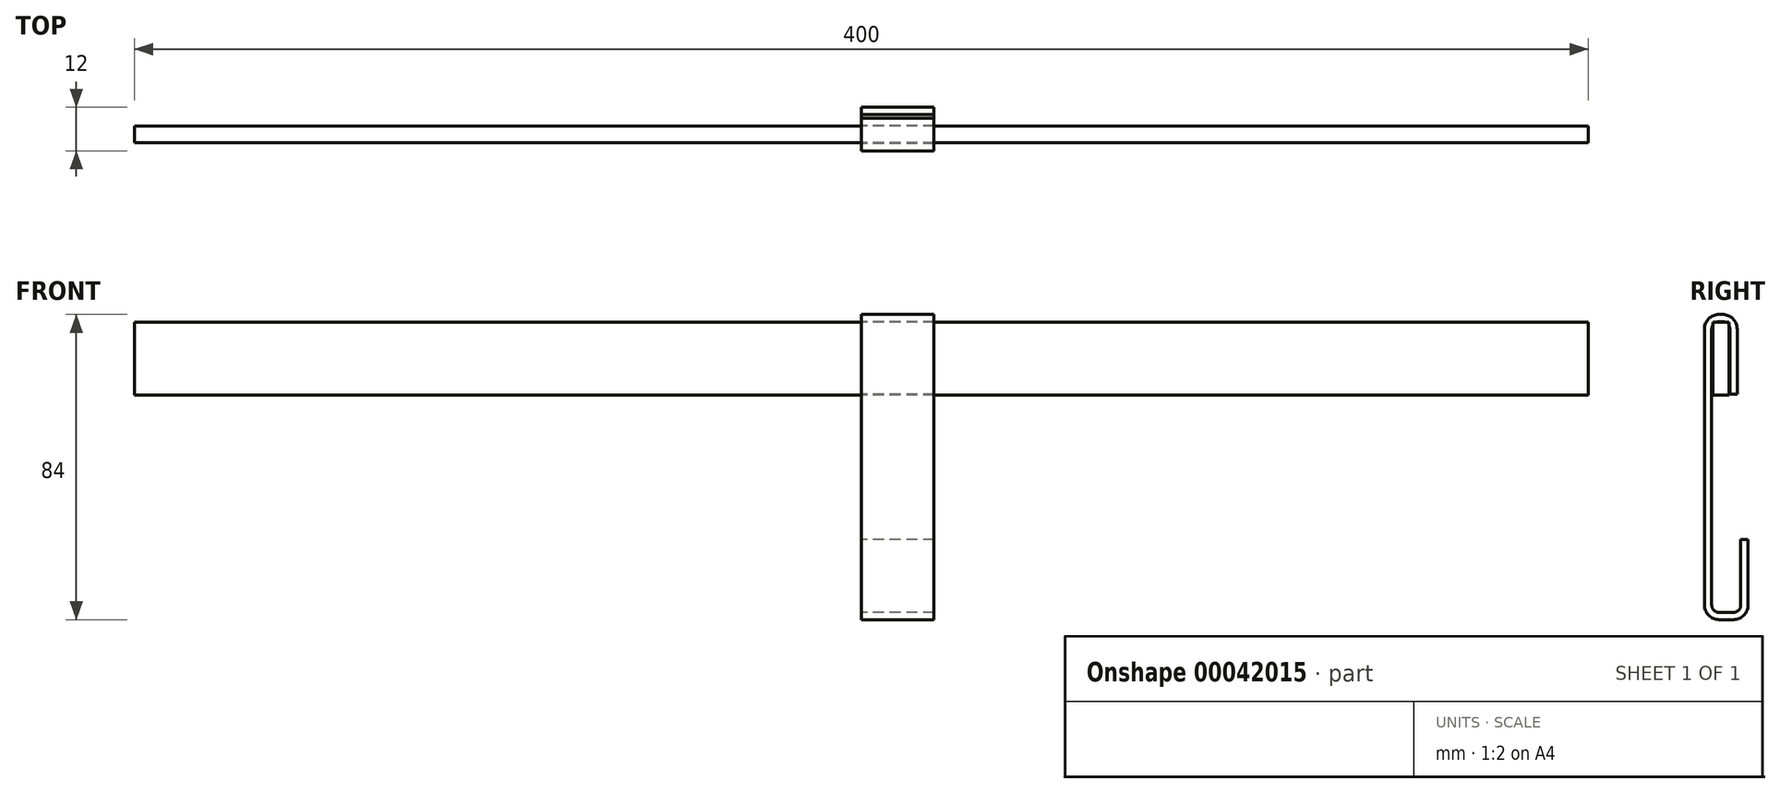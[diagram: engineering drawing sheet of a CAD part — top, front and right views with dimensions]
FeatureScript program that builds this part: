
annotation { "Feature Type Name" : "Feature", "Feature Type Description" : "" }
export const myFeature = defineFeature(function(context is Context, id is Id, definition is map)
    precondition{}
    {
        {
            var Q0;
            Q0=qCreatedBy(makeId("Right.planeOp"),FACE);
            var sketch = newSketch(context, id + "F0", { "sketchPlane" : qUnion([Q0])});
            skLineSegment(sketch, "E0", {"start": v(0, 0) * mm, "end": v(0, -80) * mm});
            skLineSegment(sketch, "E1", {"start": v(8, -80) * mm, "end": v(8, -60) * mm});
            skLineSegment(sketch, "E2", {"start": v(0, 0) * mm, "end": v(5, 0) * mm});
            skLineSegment(sketch, "E3", {"start": v(5, 0) * mm, "end": v(5, -20) * mm});
            skLineSegment(sketch, "E4", {"start": v(0, -80) * mm, "end": v(8, -80) * mm});
            skLineSegment(sketch, "E5.0", {"start": v(7, 2) * mm, "end": v(7, -20) * mm});
            skLineSegment(sketch, "E5.1", {"start": v(10, -82) * mm, "end": v(10, -60) * mm});
            skLineSegment(sketch, "E5.2", {"start": v(-2, -82) * mm, "end": v(10, -82) * mm});
            skLineSegment(sketch, "E5.3", {"start": v(-2, 2) * mm, "end": v(-2, -82) * mm});
            skLineSegment(sketch, "E5.4", {"start": v(-2, 2) * mm, "end": v(7, 2) * mm});
            skLineSegment(sketch, "E6", {"start": v(10, -60) * mm, "end": v(8, -60) * mm});
            skLineSegment(sketch, "E7", {"start": v(7, -20) * mm, "end": v(5, -20) * mm});
            skSolve(sketch);
        }
        {
            var Q0;
            Q0=makeQuery(id+"F0.imprint","IMPRINT",FACE,{"disambiguationData":[TD([[makeQuery(id+"F0.imprint","IMPRINT",EDGE,{"derivedFrom":sQuery(id+"F0.wireOp",EDGE,"E0")}),-1.0]])]});
            extrude(context, id + "F1", {"entities" : qUnion([Q0]), "depth" : 20 * mm});
        }
        {
            var Q0;
            Q0=makeQuery(id+"F1.opExtrude","SWEPT_EDGE",EDGE,{"disambiguationData":[OSD([sQuery(id+"F0.wireOp",EDGE,"E5.3"),sQuery(id+"F0.wireOp",EDGE,"E5.4")])]});
            var Q1;
            Q1=makeQuery(id+"F1.opExtrude","SWEPT_EDGE",EDGE,{"disambiguationData":[OSD([sQuery(id+"F0.wireOp",EDGE,"E5.0"),sQuery(id+"F0.wireOp",EDGE,"E5.4")])]});
            var Q2;
            Q2=makeQuery(id+"F1.opExtrude","SWEPT_EDGE",EDGE,{"disambiguationData":[OSD([sQuery(id+"F0.wireOp",EDGE,"E5.2"),sQuery(id+"F0.wireOp",EDGE,"E5.3")])]});
            var Q3;
            Q3=makeQuery(id+"F1.opExtrude","SWEPT_EDGE",EDGE,{"disambiguationData":[OSD([sQuery(id+"F0.wireOp",EDGE,"E5.1"),sQuery(id+"F0.wireOp",EDGE,"E5.2")])]});
            fillet(context, id + "F2", {"entities" : qUnion([Q0, Q1, Q2, Q3]), "radius" : 4 * mm, "tangentPropagation" : true, "allowEdgeOverflow" : false});
        }
        {
            var Q0;
            Q0=makeQuery(id+"F1.opExtrude","SWEPT_EDGE",EDGE,{"disambiguationData":[OSD([sQuery(id+"F0.wireOp",EDGE,"E1"),sQuery(id+"F0.wireOp",EDGE,"E4")])]});
            var Q1;
            Q1=makeQuery(id+"F1.opExtrude","SWEPT_EDGE",EDGE,{"disambiguationData":[OSD([sQuery(id+"F0.wireOp",EDGE,"E2"),sQuery(id+"F0.wireOp",EDGE,"E3")])]});
            var Q2;
            Q2=makeQuery(id+"F1.opExtrude","SWEPT_EDGE",EDGE,{"disambiguationData":[OSD([sQuery(id+"F0.wireOp",EDGE,"E0"),sQuery(id+"F0.wireOp",EDGE,"E2")])]});
            var Q3;
            Q3=makeQuery(id+"F1.opExtrude","SWEPT_EDGE",EDGE,{"disambiguationData":[OSD([sQuery(id+"F0.wireOp",EDGE,"E0"),sQuery(id+"F0.wireOp",EDGE,"E4")])]});
            fillet(context, id + "F3", {"entities" : qUnion([Q0, Q1, Q2, Q3]), "radius" : 2 * mm, "tangentPropagation" : true, "allowEdgeOverflow" : false});
        }
        {
            var Q0;
            Q0=qCreatedBy(makeId("Right.planeOp"),FACE);
            var sketch = newSketch(context, id + "F4", { "sketchPlane" : qUnion([Q0])});
            skLineSegment(sketch, "E8.bottom", {"start": v(0.28, -0.19) * mm, "end": v(4.78, -0.19) * mm});
            skLineSegment(sketch, "E8.top", {"start": v(0.28, -20.19) * mm, "end": v(4.78, -20.19) * mm});
            skLineSegment(sketch, "E8.left", {"start": v(0.28, -0.19) * mm, "end": v(0.28, -20.19) * mm});
            skLineSegment(sketch, "E8.right", {"start": v(4.78, -0.19) * mm, "end": v(4.78, -20.19) * mm});
            skSolve(sketch);
        }
        {
            var Q0;
            Q0=makeQuery(id+"F4.imprint","IMPRINT",FACE,{"disambiguationData":[TD([[makeQuery(id+"F4.imprint","IMPRINT",EDGE,{"derivedFrom":sQuery(id+"F4.wireOp",EDGE,"E8.bottom")}),-1.0]])]});
            extrude(context, id + "F5", {"entities" : qUnion([Q0]), "depth" : 200 * mm, "hasSecondDirection" : true, "secondDirectionOppositeDirection" : true, "secondDirectionDepth" : 200 * mm});
        }
    });
